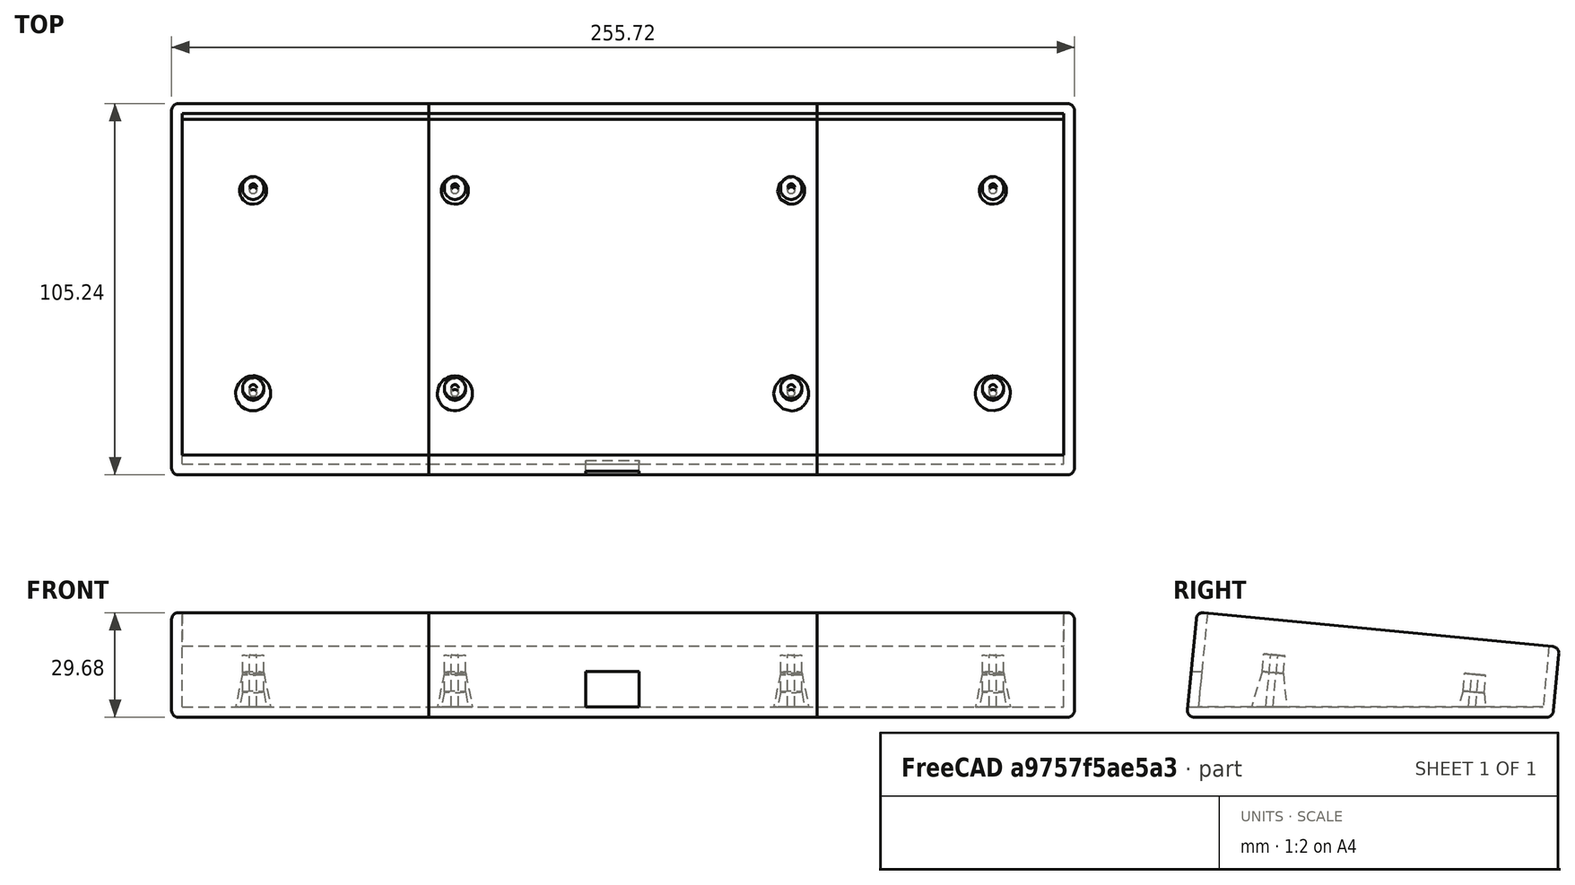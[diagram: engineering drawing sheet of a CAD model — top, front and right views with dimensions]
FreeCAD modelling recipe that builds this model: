
FCSTD DOCUMENT  (FreeCAD 0.17R13522 (Git))
Label: sloped_case
License: All rights reserved
LicenseURL: http://en.wikipedia.org/wiki/All_rights_reserved
objects: Part::Cylinder×16, Part::MultiFuse×11, Part::Cut×11, Part::Cone×8, Part::Box×7, Part::MultiCommon×3, Part::RuledSurface×1, Part::Extrusion×1, Part::Fillet×1
note: 59 computed .brp shape members not serialized (recipe doc carries the construction recipe); baked Part::Feature solids carry a one-line shape summary decoded from their .brp

FEATURE [Part::Cone] Cone  label="post_support"
  Angle = 360
  AttacherType = Attacher::AttachEngine3D
  Height = 15
  Radius1 = 6
  Radius2 = 3
FEATURE [Part::Cylinder] Cylinder  label="post_hole"
  Angle = 360
  AttacherType = Attacher::AttachEngine3D
  Height = 20
  Radius = 0.985
FEATURE [Part::Cylinder] Cylinder001  label="post_wall"
  Angle = 360
  AttacherType = Attacher::AttachEngine3D
  Height = 20
  Radius = 3
FEATURE [Part::MultiFuse] Fusion
  Shapes = -> [Cone,Cylinder001]
FEATURE [Part::Cut] Cut  label="post"
  Base = -> Fusion
  Tool = -> Cylinder
FEATURE [Part::Cone] Cone001  label="post_support001"
  Angle = 360
  AttacherType = Attacher::AttachEngine3D
  Height = 15
  Radius1 = 6
  Radius2 = 3
FEATURE [Part::Cylinder] Cylinder002  label="post_hole001"
  Angle = 360
  AttacherType = Attacher::AttachEngine3D
  Height = 20
  Radius = 0.985
FEATURE [Part::Cylinder] Cylinder003  label="post_wall001"
  Angle = 360
  AttacherType = Attacher::AttachEngine3D
  Height = 20
  Radius = 3
FEATURE [Part::MultiFuse] Fusion001
  Shapes = -> [Cone001,Cylinder003]
FEATURE [Part::Cut] Cut001  label="post001"
  Base = -> Fusion001
  Placement = pos=(57.15,0,0) rot=(0,0,1;0rad)
  Tool = -> Cylinder002
FEATURE [Part::Cone] Cone002  label="post_support002"
  Angle = 360
  AttacherType = Attacher::AttachEngine3D
  Height = 15
  Radius1 = 6
  Radius2 = 3
FEATURE [Part::Cylinder] Cylinder004  label="post_hole002"
  Angle = 360
  AttacherType = Attacher::AttachEngine3D
  Height = 20
  Radius = 0.985
FEATURE [Part::Cylinder] Cylinder005  label="post_wall002"
  Angle = 360
  AttacherType = Attacher::AttachEngine3D
  Height = 20
  Radius = 3
FEATURE [Part::MultiFuse] Fusion002
  Shapes = -> [Cone002,Cylinder005]
FEATURE [Part::Cut] Cut002  label="post002"
  Base = -> Fusion002
  Placement = pos=(0,57.15,0) rot=(0,0,1;0rad)
  Tool = -> Cylinder004
FEATURE [Part::Cone] Cone003  label="post_support003"
  Angle = 360
  AttacherType = Attacher::AttachEngine3D
  Height = 15
  Radius1 = 6
  Radius2 = 3
FEATURE [Part::Cylinder] Cylinder006  label="post_hole003"
  Angle = 360
  AttacherType = Attacher::AttachEngine3D
  Height = 20
  Radius = 0.985
FEATURE [Part::Cylinder] Cylinder007  label="post_wall003"
  Angle = 360
  AttacherType = Attacher::AttachEngine3D
  Height = 20
  Radius = 3
FEATURE [Part::MultiFuse] Fusion003
  Shapes = -> [Cone003,Cylinder007]
FEATURE [Part::Cut] Cut003  label="post003"
  Base = -> Fusion003
  Placement = pos=(57.15,57.15,0) rot=(0,0,1;0rad)
  Tool = -> Cylinder006
FEATURE [Part::Cone] Cone004  label="post_support004"
  Angle = 360
  AttacherType = Attacher::AttachEngine3D
  Height = 15
  Radius1 = 6
  Radius2 = 3
FEATURE [Part::Cylinder] Cylinder008  label="post_hole004"
  Angle = 360
  AttacherType = Attacher::AttachEngine3D
  Height = 20
  Radius = 0.985
FEATURE [Part::Cylinder] Cylinder009  label="post_wall004"
  Angle = 360
  AttacherType = Attacher::AttachEngine3D
  Height = 20
  Radius = 3
FEATURE [Part::MultiFuse] Fusion004
  Shapes = -> [Cone004,Cylinder009]
FEATURE [Part::Cut] Cut004  label="post004"
  Base = -> Fusion004
  Placement = pos=(152.4,0,0) rot=(0,0,1;0rad)
  Tool = -> Cylinder008
FEATURE [Part::Cone] Cone005  label="post_support005"
  Angle = 360
  AttacherType = Attacher::AttachEngine3D
  Height = 15
  Radius1 = 6
  Radius2 = 3
FEATURE [Part::Cylinder] Cylinder010  label="post_hole005"
  Angle = 360
  AttacherType = Attacher::AttachEngine3D
  Height = 20
  Radius = 0.985
FEATURE [Part::Cylinder] Cylinder011  label="post_wall005"
  Angle = 360
  AttacherType = Attacher::AttachEngine3D
  Height = 20
  Radius = 3
FEATURE [Part::MultiFuse] Fusion005
  Shapes = -> [Cone005,Cylinder011]
FEATURE [Part::Cut] Cut005  label="post005"
  Base = -> Fusion005
  Placement = pos=(209.55,0,0) rot=(0,0,1;0rad)
  Tool = -> Cylinder010
FEATURE [Part::Cone] Cone006  label="post_support006"
  Angle = 360
  AttacherType = Attacher::AttachEngine3D
  Height = 15
  Radius1 = 6
  Radius2 = 3
FEATURE [Part::Cylinder] Cylinder012  label="post_hole006"
  Angle = 360
  AttacherType = Attacher::AttachEngine3D
  Height = 20
  Radius = 0.985
FEATURE [Part::Cylinder] Cylinder013  label="post_wall006"
  Angle = 360
  AttacherType = Attacher::AttachEngine3D
  Height = 20
  Radius = 3
FEATURE [Part::MultiFuse] Fusion006
  Shapes = -> [Cone006,Cylinder013]
FEATURE [Part::Cut] Cut006  label="post006"
  Base = -> Fusion006
  Placement = pos=(152.4,57.15,0) rot=(0,0,1;0rad)
  Tool = -> Cylinder012
FEATURE [Part::Cone] Cone007  label="post_support007"
  Angle = 360
  AttacherType = Attacher::AttachEngine3D
  Height = 15
  Radius1 = 6
  Radius2 = 3
FEATURE [Part::Cylinder] Cylinder014  label="post_hole007"
  Angle = 360
  AttacherType = Attacher::AttachEngine3D
  Height = 20
  Radius = 0.985
FEATURE [Part::Cylinder] Cylinder015  label="post_wall007"
  Angle = 360
  AttacherType = Attacher::AttachEngine3D
  Height = 20
  Radius = 3
FEATURE [Part::MultiFuse] Fusion007
  Shapes = -> [Cone007,Cylinder015]
FEATURE [Part::Cut] Cut007  label="post007"
  Base = -> Fusion007
  Placement = pos=(209.55,57.15,0) rot=(0,0,1;0rad)
  Tool = -> Cylinder014
FEATURE [Part::MultiFuse] Fusion008  label="posts"
  Placement = pos=(23.09,23.03,0) rot=(0,0,1;0rad)
  Shapes = -> [Cut,Cut002,Cut001,Cut003,Cut004,Cut005,Cut006,Cut007]
FEATURE [Part::Box] Box  label="wall_block"
  AttacherType = Attacher::AttachEngine3D
  Height = 30
  Length = 255.72
  Width = 103.21
FEATURE [Part::Box] Box001  label="cable_hole"
  AttacherType = Attacher::AttachEngine3D
  Height = 10
  Length = 15
  Placement = pos=(117.36,0,3) rot=(0,0,1;0rad)
  Width = 5
FEATURE [Part::Box] Box002  label="wall_hole"
  AttacherType = Attacher::AttachEngine3D
  Height = 30
  Length = 249.72
  Placement = pos=(3,3,0) rot=(0,0,1;0rad)
  Width = 97.21
FEATURE [Part::Box] Box003  label="Cube"
  AttacherType = Attacher::AttachEngine3D
  Height = 30
  Length = 255.72
  Placement = pos=(0,0,-30) rot=(0,0,1;0rad)
  Width = 105.62
FEATURE [Part::Cut] Cut008
  Base = -> Box
  Tool = -> Box002
FEATURE [Part::MultiFuse] Fusion009
  Placement = pos=(0,0,0) rot=(-1,0,0;0.096517rad)
  Shapes = -> [Fusion008,Cut008]
FEATURE [Part::Cut] Cut009
  Base = -> Fusion009
  Tool = -> Box003
FEATURE [Part::Cut] Cut010
  Base = -> Cut009
  Tool = -> Box001
FEATURE [Part::RuledSurface] Ruled_Surface
  Curve1 = -> Cut010 [Edge85]
  Curve2 = -> Cut010 [Edge87]
  Orientation = 0
FEATURE [Part::Extrusion] Extrude  label="case"
  Base = -> Ruled_Surface
  Dir = (0,1.95605,20.2034)
  DirLink = -> Cut010 [Edge98]
  DirMode = 1
  FaceMakerClass = Part::FaceMakerBullseye
  LengthFwd = 3
  LengthRev = 0
  Solid = false
  Symmetric = false
FEATURE [Part::MultiFuse] Fusion010  label="case001"
  Shapes = -> [Extrude,Cut010]
FEATURE [Part::Fillet] Fillet
  Base = -> Fusion010
  Edges = 12 edges r=2: [Edge55,Edge56,Edge57,Edge58,Edge81,Edge82,Edge83,Edge84,Edge85,Edge86,Edge87,Edge88]
FEATURE [Part::Box] Box004  label="Cube001"
  AttacherType = Attacher::AttachEngine3D
  Height = 30
  Length = 72.875
  Placement = pos=(182.88,0,0) rot=(0,0,1;0rad)
  Width = 106
FEATURE [Part::Box] Box005  label="Cube002"
  AttacherType = Attacher::AttachEngine3D
  Height = 30
  Length = 110
  Placement = pos=(72.88,0,0) rot=(0,0,1;0rad)
  Width = 106
FEATURE [Part::Box] Box006  label="Cube003"
  AttacherType = Attacher::AttachEngine3D
  Height = 30
  Length = 72.875
  Width = 106
FEATURE [Part::MultiCommon] Common  label="left"
  Shapes = -> [Fillet,Box004]
FEATURE [Part::MultiCommon] Common001  label="right"
  Shapes = -> [Fillet,Box006]
FEATURE [Part::MultiCommon] Common002  label="center"
  Shapes = -> [Fillet,Box005]
